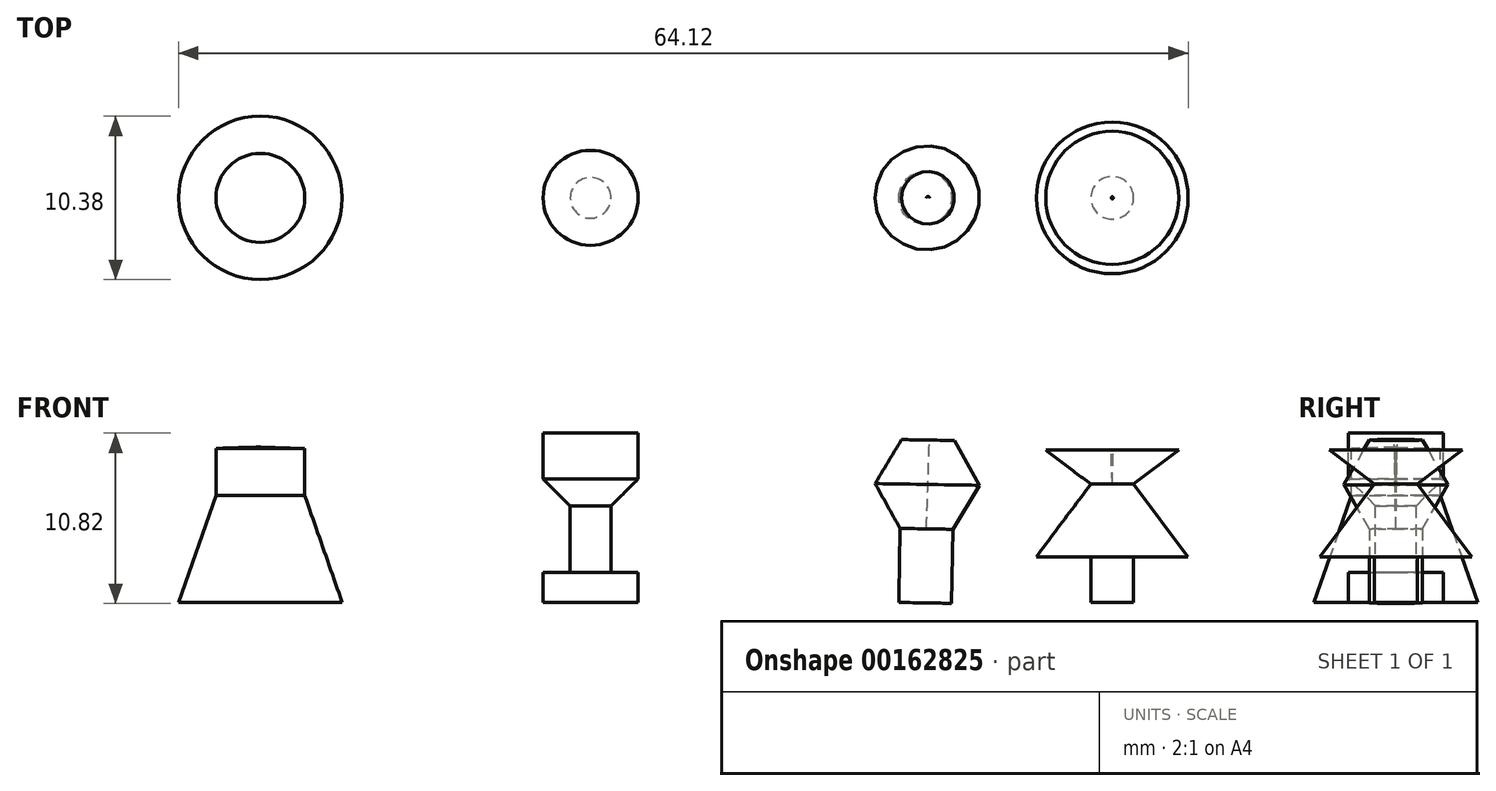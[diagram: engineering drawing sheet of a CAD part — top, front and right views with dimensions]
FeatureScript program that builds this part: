
annotation { "Feature Type Name" : "Feature", "Feature Type Description" : "" }
export const myFeature = defineFeature(function(context is Context, id is Id, definition is map)
    precondition{}
    {
        {
            var Q0;
            Q0=qCreatedBy(makeId("Front.planeOp"),FACE);
            var sketch = newSketch(context, id + "F0", { "sketchPlane" : qUnion([Q0])});
            skLineSegment(sketch, "E0", {"start": v(-39.48, 0) * mm, "end": v(-37.11, 6.78) * mm});
            skLineSegment(sketch, "E1", {"start": v(-34.29, 0) * mm, "end": v(-39.48, 0) * mm});
            skLineSegment(sketch, "E2.0", {"start": v(-37.11, 9.78) * mm, "end": v(-34.29, 9.87) * mm});
            skLineSegment(sketch, "E3", {"start": v(-37.11, 9.78) * mm, "end": v(-37.11, 6.78) * mm});
            skLineSegment(sketch, "E4", {"start": v(-34.29, 9.87) * mm, "end": v(-34.29, 0) * mm});
            skSolve(sketch);
        }
        {
            var Q0;
            Q0=makeQuery(id+"F0.imprint","IMPRINT",FACE,{"disambiguationData":[TD([[makeQuery(id+"F0.imprint","IMPRINT",EDGE,{"derivedFrom":sQuery(id+"F0.wireOp",EDGE,"E0")}),-1.0]])]});
            var Q1;
            Q1=sQuery(id+"F0.wireOp",EDGE,"E4");
            revolve(context, id + "F1", {"entities" : qUnion([Q0]), "axis" : qUnion([Q1]), "revolveType" : RevolveType.FULL});
        }
        {
            var Q0;
            Q0=qCreatedBy(makeId("Front.planeOp"),FACE);
            var sketch = newSketch(context, id + "F2", { "sketchPlane" : qUnion([Q0])});
            skLineSegment(sketch, "E5", {"start": v(-16.33, 0) * mm, "end": v(-16.33, 1.92) * mm});
            skLineSegment(sketch, "E6", {"start": v(-16.33, 1.92) * mm, "end": v(-14.6, 1.92) * mm});
            skLineSegment(sketch, "E7", {"start": v(-14.6, 1.92) * mm, "end": v(-14.6, 6.12) * mm});
            skLineSegment(sketch, "E8", {"start": v(-14.6, 6.12) * mm, "end": v(-16.33, 7.85) * mm});
            skLineSegment(sketch, "E9", {"start": v(-16.33, 7.85) * mm, "end": v(-16.33, 10.76) * mm});
            skLineSegment(sketch, "E10", {"start": v(-16.33, 10.76) * mm, "end": v(-13.31, 10.76) * mm});
            skLineSegment(sketch, "E11", {"start": v(-13.31, 10.76) * mm, "end": v(-13.31, 0) * mm});
            skLineSegment(sketch, "E12", {"start": v(-13.31, 0) * mm, "end": v(-16.33, 0) * mm});
            skSolve(sketch);
        }
        {
            var Q0;
            Q0=makeQuery(id+"F2.imprint","IMPRINT",FACE,{"disambiguationData":[TD([[makeQuery(id+"F2.imprint","IMPRINT",EDGE,{"derivedFrom":sQuery(id+"F2.wireOp",EDGE,"E5")}),-1.0]])]});
            var Q1;
            Q1=sQuery(id+"F2.wireOp",EDGE,"E11");
            revolve(context, id + "F3", {"entities" : qUnion([Q0]), "axis" : qUnion([Q1]), "revolveType" : RevolveType.FULL});
        }
        {
            var Q0;
            Q0=qCreatedBy(makeId("Front.planeOp"),FACE);
            var sketch = newSketch(context, id + "F4", { "sketchPlane" : qUnion([Q0])});
            skLineSegment(sketch, "E13.2", {"start": v(6.34, 4.7) * mm, "end": v(4.76, 7.55) * mm});
            skLineSegment(sketch, "E13.3", {"start": v(4.76, 7.55) * mm, "end": v(6.43, 10.34) * mm});
            skLineSegment(sketch, "E14", {"start": v(6.34, 4.7) * mm, "end": v(6.26, 0) * mm});
            skLineSegment(sketch, "E15", {"start": v(6.26, 0) * mm, "end": v(7.94, -0.03) * mm});
            skLineSegment(sketch, "E16", {"start": v(7.94, -0.03) * mm, "end": v(8.02, 4.67) * mm});
            skLineSegment(sketch, "E17", {"start": v(8.02, 4.67) * mm, "end": v(8.02, 7.5) * mm});
            skLineSegment(sketch, "E18", {"start": v(8.02, 7.5) * mm, "end": v(8.02, 10.32) * mm});
            skLineSegment(sketch, "E19", {"start": v(6.43, 10.34) * mm, "end": v(8.02, 10.32) * mm});
            skSolve(sketch);
        }
        {
            var Q0;
            Q0=makeQuery(id+"F4.imprint","IMPRINT",FACE,{"disambiguationData":[TD([[makeQuery(id+"F4.imprint","IMPRINT",EDGE,{"derivedFrom":sQuery(id+"F4.wireOp",EDGE,"E13.2")}),-1.0]])]});
            var Q1;
            Q1=sQuery(id+"F4.wireOp",EDGE,"E16");
            revolve(context, id + "F5", {"entities" : qUnion([Q0]), "axis" : qUnion([Q1]), "revolveType" : RevolveType.FULL});
        }
        {
            var Q0;
            Q0=qCreatedBy(makeId("Front.planeOp"),FACE);
            var sketch = newSketch(context, id + "F6", { "sketchPlane" : qUnion([Q0])});
            skLineSegment(sketch, "E20.bottom", {"start": v(19.82, 0) * mm, "end": v(21.17, 0) * mm});
            skLineSegment(sketch, "E20.top", {"start": v(19.82, 7.52) * mm, "end": v(21.17, 7.52) * mm});
            skLineSegment(sketch, "E20.left", {"start": v(19.82, 0) * mm, "end": v(19.82, 7.52) * mm});
            skLineSegment(sketch, "E20.right", {"start": v(21.17, 0) * mm, "end": v(21.17, 7.52) * mm});
            skLineSegment(sketch, "E21", {"start": v(21.17, 7.52) * mm, "end": v(24.64, 2.9) * mm});
            skLineSegment(sketch, "E22", {"start": v(24.64, 2.9) * mm, "end": v(21.17, 2.9) * mm});
            skLineSegment(sketch, "E23", {"start": v(21.17, 7.52) * mm, "end": v(24.04, 9.67) * mm});
            skLineSegment(sketch, "E24", {"start": v(24.04, 9.67) * mm, "end": v(19.88, 9.67) * mm});
            skLineSegment(sketch, "E25", {"start": v(19.88, 9.67) * mm, "end": v(19.82, 7.52) * mm});
            skSolve(sketch);
        }
        {
            var Q0;
            {var subQ1=sQuery(id+"F6.wireOp",EDGE,"E20.bottom");Q0=makeQuery(id+"F6.imprint","IMPRINT",FACE,{"disambiguationData":[TD([[makeQuery(id+"F6.imprint","IMPRINT",EDGE,{"derivedFrom":subQ1}),1.0]])]});}
            var Q1;
            {var subQ0=sQuery(id+"F6.wireOp",EDGE,"E21");Q1=makeQuery(id+"F6.imprint","IMPRINT",FACE,{"disambiguationData":[TD([[makeQuery(id+"F6.imprint","IMPRINT",EDGE,{"derivedFrom":subQ0}),-1.0]])]});}
            var Q2;
            Q2=makeQuery(id+"F6.imprint","IMPRINT",FACE,{"disambiguationData":[TD([[makeQuery(id+"F6.imprint","IMPRINT",EDGE,{"derivedFrom":sQuery(id+"F6.wireOp",EDGE,"E20.top")}),1.0]])]});
            var Q3;
            Q3=sQuery(id+"F6.wireOp",EDGE,"E20.left");
            revolve(context, id + "F7", {"entities" : qUnion([Q0, Q1, Q2]), "axis" : qUnion([Q3]), "revolveType" : RevolveType.FULL});
        }
    });
